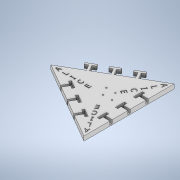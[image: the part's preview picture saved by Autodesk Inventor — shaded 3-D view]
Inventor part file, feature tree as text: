
AUTODESK INVENTOR PART (.ipt)
format: ipt  version: 2022.3 (Build 263350000, 350)  size: 703,488 bytes
history: native  units: mm
features: extrude x6, thicken_offset x6, sketch x5, hole x1, emboss x1, pattern_circular x1, projected_geometry x1
ambient origin geometry x8: Origin, YZ Plane, XZ Plane, XY Plane, X Axis, Y Axis, Z Axis, Center Point
bodies: Solid1 (feature_tree)
feature tree (21):
  sketch  "Sketch1"  dims[d1=200.0mm d2=35.0mm]
  extrude  "Extrusion1"  Depth=35.0mm
  extrude  "Extrusion2"  Depth=5.0mm
  extrude  "Extrusion3"  Depth=30.0mm
  extrude  "Extrusion4"  Depth=10.0mm TaperAngle=0.0deg
  sketch  "Sketch3"  dims[d5=20.0mm d6=30.0mm d8=40.0mm d9=30.0mm d11=40.0mm]
  extrude  "Extrusion6"  Depth=10.0mm
  extrude  "Extrusion7"  Depth=10.0mm
  hole  "Hole1"  [1 undecoded]
  thicken_offset  "Thicken1"
  thicken_offset  "Thicken2"
  thicken_offset  "Thicken3"
  thicken_offset  "Thicken4"
  thicken_offset  "Thicken5"
  thicken_offset  "Thicken6"
  emboss  "Emboss1"
  pattern_circular  "Circular Pattern1"  [2 undecoded]
  sketch  "Sketch2"  dims[d3=5.0mm d4=5.0mm]
  projected_geometry  "Projected Loop1"
  sketch  "Sketch4"  dims[d14=10.0mm d15=0.0mm d16=10.0mm d17=0.0mm]
  sketch  "Sketch5"  dims[d18=2.2mm d19=0.0mm d20=22.0mm d21=3.0mm d22=1.5mm d23=0.0mm d24=15.0mm d25=120.0deg d26=10.0mm d27=5.0mm d28=20.0mm d29=90.0deg d30=5.0mm d31=2.5mm d32=5.0mm d33=20.0mm d35=120.0deg d37=30.0mm d39=40.0mm d40=30.0mm d42=40.0mm d45=30.0mm d47=40.0mm d48=30.0mm d50=40.0mm d55=7.8mm d56=0.0mm d57=10.0mm d58=0.0mm d59=40.0mm d60=2.2mm d61=6.0mm d62=3.1mm d63=4.1mm d64=90.0deg d65=2.2mm d66=0.0mm d67=0.1mm d68=0.05mm d69=0.1mm d70=0.05mm d71=0.1mm d72=0.05mm d73=0.1mm d74=0.05mm d75=0.1mm d76=0.05mm d77=0.1mm d78=0.05mm d79=1.0mm d80=0.0mm d81=30.0mm d82=360.0deg d84=16.0mm d85=2.0mm d86=0.0mm d87=8.0mm d88=10.0mm d89=50.0mm d90=50.0mm d91=50.0mm d92=50.0mm d93=90.0deg d94=50.0mm d95=50.0mm]
note: 3 required parameter values undecoded (feature->parameter linkage not recoverable at this tier; creation-order binding heuristic only, values carry confidence <= 0.55)
